# Revit family: PURY-EP750YSNW-A1
name_source: partatom
category: 機械設備
revit_build: Autodesk Revit 2016 (Build: 20150220_1215(x64)
units: mm (PartAtom-declared; Revit-internal decimal feet)

## family parameters
OmniClass タイトル = Climate Control (HVAC)
OmniClass 番号 = 23.75.00.00
パーツ タイプ = 標準
ロード時にボイドで切り取り = いいえ
丸型コネクタ寸法 = 半径を使用
作業面に基づく = いいえ
共有 = いいえ
常に垂直 = はい
部屋の計算ポイント = いいえ

## types (6) — shared parameters
Airflow Rate (m3/h) = 33900
Airflow Rate (m3/min) = 565
Compressor Motor Output (kW) = 19.5
Compressor_Lubricant = MEL32
Compressor_Quantity = 2
Compressor_Type = Inverter scroll hermetic compressor
Cooling Capacity (kW) = 85
Cooling EER (kW/kW) = 3.62
Cooling Power Input (kW) = 23.48
Cooling SEER (kW/kW) = 6.49
Depth = 740  [stored 2.42782 ft]
External Finish = Pre-coated galvanized steel sheets (+powder coating for -BS type) <MUNSELL 5Y 8/1 or similar>
Fan Motor Output (kW) = 1.84
Fan_Quantity = 4
Fan_Type = Propeller Fan
Heating COP (Nominal) (kW/kW) = 4.01
Heating COP (kW/kW) = 3.75
Heating Capacity (Nominal) (kW) = 85
Heating Capacity (kW) = 95
Heating Power Input (Nominal) (kW) = 21.19
Heating Power Input (kW) = 25.33
Heating SCOP (kW/kW) = 3.99
Height = 1858  [stored 6.0958 ft]
High pressure pipe_radius = 14.29  [stored 0.0468832 ft]
Indoor Unit Model/Quantity = P10 to P250/2 to 50
Indoor Unit Total Capacity = 50 to 150% of outdoor unit capacity
Low pressure pipe_radius = 17.465  [stored 0.0572999 ft]
Maximum Circuit Ampacity (A) = 55.1
Note_1 = Refrigerant pipe diameters may change depending on the installation condition. Please refer to the installation manual.
Outdoor unit 1 = PURY-EP400YNW-A1
Outdoor unit 1 Breaker size (A) = 60
Outdoor unit 2 = PURY-EP350YNW-A1
Outdoor unit 2 Breaker size (A) = 40
Phase = 3
Protection Devices_High pressure (MPa) = High pressure sensor, High pressure switch at 4.15
Protection Devices_Inverter circuit (COMP./FAN) = Over-current protection
Refrigerant Charge (kg) = 16
Refrigerant type = R410A
Sound Pressure Level (dB(A)) Cooling mode = 67
Sound Pressure Level (dB(A)) Heating mode = 70.5
Space View = はい
Subcategory = HVAC
Temp. range of cooling (Indoor temp.) (W.B.) = 15.0 to 24.0
Temp. range of cooling (Outdoor temp.) (D.B.) = -5.0 to 52.0
Temp. range of heating (Indoor temp.) (D.B.) = 15.0 to 27.0
Temp. range of heating (Outdoor temp.) (W.B.) = -20.0 to 15.5
URL = http://www.mitsubishielectric.com
Unit Weight (kg) = 551
Width = 2510  [stored 8.23491 ft]
モデル = PURY-EP750YSNW-A1
製造元 = Mitsubishi Electric Corporation
zero-valued in all types: Equip_No., External static pressure (Pa), SerialNumber, TagNumber

## per-type parameters (varying)
| type | AssetIdentifier | Barcode | Category | Cooling Current Input (A) | Cooling Rated Load Ampacity (A) | Description | Equip_ID | Equip_description | Heating Current Input (A) | Heating Current Input (Nominal) (A) | Heating Rated Load Ampacity (A) | Hertz | InstallationDate | Voltage |
| PURY-EP750YSNW-A1_380V_50Hz |  |  |  | 39.6 | 39.6 |  |  |  | 42.7 | 35.7 | 42.7 | 50 Hz |  | 380 V |
| PURY-EP750YSNW-A1_380V_60Hz | 0 | 0 | 0 | 39.6 | 39.6 | 0 | 0 | 0 | 42.7 | 35.7 | 42.7 | 60 Hz | 0 | 380 V |
| PURY-EP750YSNW-A1_400V_50Hz | 0 | 0 | 0 | 37.6 | 37.6 | 0 | 0 | 0 | 40.6 | 33.9 | 40.6 | 50 Hz | 0 | 400 V |
| PURY-EP750YSNW-A1_400V_60Hz | 0 | 0 | 0 | 37.6 | 37.6 | 0 | 0 | 0 | 40.6 | 33.9 | 40.6 | 60 Hz | 0 | 400 V |
| PURY-EP750YSNW-A1_415V_50Hz | 0 | 0 | 0 | 36.2 | 36.2 | 0 | 0 | 0 | 39.1 | 32.7 | 39.1 | 50 Hz | 0 | 415 V |
| PURY-EP750YSNW-A1_415V_60Hz | 0 | 0 | 0 | 36.2 | 36.2 | 0 | 0 | 0 | 39.1 | 32.7 | 39.1 | 60 Hz | 0 | 415 V |

note: [stored X ft] marks values corroborated as IEEE doubles in the binary element streams (Revit-internal decimal feet)

## geometry (parser evidence)
native form markers: Blend x80, Sweep x15
no freeform markers — native parametric forms only
